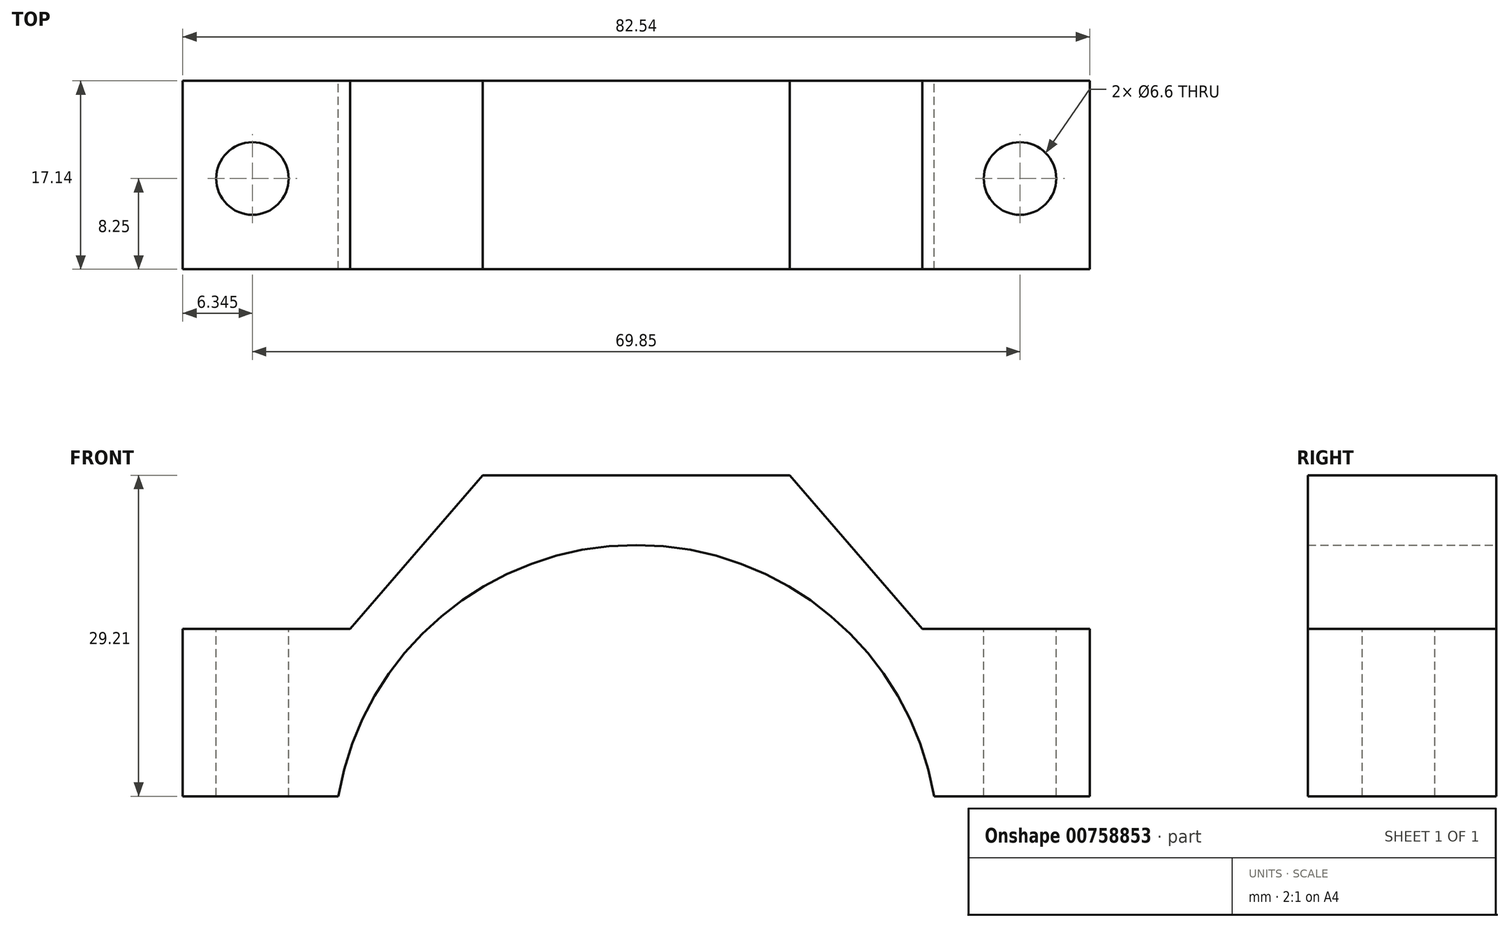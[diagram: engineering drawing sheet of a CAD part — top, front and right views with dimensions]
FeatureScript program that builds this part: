
annotation { "Feature Type Name" : "Feature", "Feature Type Description" : "" }
export const myFeature = defineFeature(function(context is Context, id is Id, definition is map)
    precondition{}
    {
        {
            var Q0;
            Q0=qCreatedBy(makeId("Front.planeOp"),FACE);
            var sketch = newSketch(context, id + "F0", { "sketchPlane" : qUnion([Q0])});
            skLineSegment(sketch, "E0", {"start": v(0, 0) * mm, "end": v(44.45, 0) * mm});
            skLineSegment(sketch, "E1", {"start": v(44.45, 0) * mm, "end": v(44.45, 17.78) * mm});
            skLineSegment(sketch, "E2", {"start": v(44.45, 17.78) * mm, "end": v(41.28, 19.05) * mm});
            skLineSegment(sketch, "E3", {"start": v(41.28, 19.05) * mm, "end": v(41.28, 52.07) * mm});
            skLineSegment(sketch, "E4", {"start": v(41.28, 52.07) * mm, "end": v(26.04, 52.07) * mm});
            skLineSegment(sketch, "E5", {"start": v(26.04, 52.07) * mm, "end": v(13.97, 66.04) * mm});
            skLineSegment(sketch, "E6", {"start": v(13.97, 66.04) * mm, "end": v(0, 66.04) * mm});
            skLineSegment(sketch, "E7.MirrorCS", {"start": v(-41.28, 19.05) * mm, "end": v(-41.28, 52.07) * mm});
            skLineSegment(sketch, "E8.MirrorCS", {"start": v(-44.45, 17.78) * mm, "end": v(-41.28, 19.05) * mm});
            skLineSegment(sketch, "E9.MirrorCS", {"start": v(-41.28, 52.07) * mm, "end": v(-26.04, 52.07) * mm});
            skLineSegment(sketch, "E10.MirrorCS", {"start": v(0, 0) * mm, "end": v(-44.45, 0) * mm});
            skLineSegment(sketch, "E11.MirrorCS", {"start": v(-13.97, 66.04) * mm, "end": v(0, 66.04) * mm});
            skLineSegment(sketch, "E12.MirrorCS", {"start": v(-26.04, 52.07) * mm, "end": v(-13.97, 66.04) * mm});
            skLineSegment(sketch, "E13.MirrorCS", {"start": v(-44.45, 0) * mm, "end": v(-44.45, 17.78) * mm});
            skCircle(sketch, "E14", {"center": v(0, 32.2) * mm, "radius": 27.5 * mm});
            skSolve(sketch);
        }
        {
            var Q0;
            Q0 = qSketchRegion(id + "F0", true);
            extrude(context, id + "F1", {"entities" : qUnion([Q0]), "depth" : 38.1 * mm, "offsetDistance" : 25.4 * mm});
        }
        {
            var Q0;
            Q0=makeQuery(id+"F1.opExtrude","CAP_FACE",FACE,{"disambiguationData":[OSD([sQuery(id+"F0.wireOp",EDGE,"E0"),sQuery(id+"F0.wireOp",EDGE,"E1"),sQuery(id+"F0.wireOp",EDGE,"E2"),sQuery(id+"F0.wireOp",EDGE,"E3"),sQuery(id+"F0.wireOp",EDGE,"E4"),sQuery(id+"F0.wireOp",EDGE,"E5"),sQuery(id+"F0.wireOp",EDGE,"E6"),sQuery(id+"F0.wireOp",EDGE,"E7.MirrorCS"),sQuery(id+"F0.wireOp",EDGE,"E8.MirrorCS"),sQuery(id+"F0.wireOp",EDGE,"E9.MirrorCS"),sQuery(id+"F0.wireOp",EDGE,"E10.MirrorCS"),sQuery(id+"F0.wireOp",EDGE,"E11.MirrorCS"),sQuery(id+"F0.wireOp",EDGE,"E12.MirrorCS"),sQuery(id+"F0.wireOp",EDGE,"E13.MirrorCS"),sQuery(id+"F0.wireOp",EDGE,"E14")])],"isStart":false});
            var sketch = newSketch(context, id + "F2", { "sketchPlane" : qUnion([Q0])});
            skLineSegment(sketch, "E15.bottom", {"start": v(-41.28, 31.75) * mm, "end": v(-22.23, 31.75) * mm});
            skLineSegment(sketch, "E15.top", {"start": v(-41.28, 36.83) * mm, "end": v(-22.23, 36.83) * mm});
            skLineSegment(sketch, "E15.left", {"start": v(-41.28, 31.75) * mm, "end": v(-41.28, 36.83) * mm});
            skLineSegment(sketch, "E15.right", {"start": v(-22.23, 31.75) * mm, "end": v(-22.23, 36.83) * mm});
            skSolve(sketch);
        }
        {
            var Q0;
            Q0 = qSketchRegion(id + "F2", true);
            extrude(context, id + "F3", {"entities" : qUnion([Q0]), "operationType" : NewBodyOperationType.REMOVE, "endBound" : BoundingType.UP_TO_NEXT, "oppositeDirection" : true, "depth" : 25.4 * mm, "offsetDistance" : 25.4 * mm});
        }
        {
            var Q0;
            Q0=makeQuery(id+"F1.opExtrude","SWEPT_FACE",FACE,{"disambiguationData":[OSD([sQuery(id+"F0.wireOp",EDGE,"E9.MirrorCS")])]});
            var sketch = newSketch(context, id + "F4", { "sketchPlane" : qUnion([Q0])});
            skLineSegment(sketch, "E16", {"start": v(-41.28, -19.05) * mm, "end": v(41.4, -19.05) * mm, "construction": true});
            skPoint(sketch, "E17", {"position": v(-34.93, -29.21) * mm});
            skPoint(sketch, "E18.MirrorP", {"position": v(-34.93, -8.89) * mm});
            skPoint(sketch, "E19.MirrorP", {"position": v(34.93, -8.89) * mm});
            skPoint(sketch, "E20.MirrorP", {"position": v(34.93, -29.21) * mm});
            skSolve(sketch);
        }
        {
            var Q0;
            Q0=sQuery(id+"F4.wireOp",VERTEX,"E18.MirrorP");
            var Q1;
            Q1=sQuery(id+"F4.wireOp",VERTEX,"E17");
            var Q2;
            Q2=sQuery(id+"F4.wireOp",VERTEX,"E19.MirrorP");
            var Q3;
            Q3=sQuery(id+"F4.wireOp",VERTEX,"E20.MirrorP");
            var Q4;
            Q4=makeQuery(id+"F1.opExtrude","SWEPT_BODY",BODY,{"disambiguationData":[OSD([sQuery(id+"F0.wireOp",EDGE,"E0"),sQuery(id+"F0.wireOp",EDGE,"E1"),sQuery(id+"F0.wireOp",EDGE,"E2"),sQuery(id+"F0.wireOp",EDGE,"E3"),sQuery(id+"F0.wireOp",EDGE,"E4"),sQuery(id+"F0.wireOp",EDGE,"E5"),sQuery(id+"F0.wireOp",EDGE,"E6"),sQuery(id+"F0.wireOp",EDGE,"E7.MirrorCS"),sQuery(id+"F0.wireOp",EDGE,"E8.MirrorCS"),sQuery(id+"F0.wireOp",EDGE,"E9.MirrorCS"),sQuery(id+"F0.wireOp",EDGE,"E10.MirrorCS"),sQuery(id+"F0.wireOp",EDGE,"E11.MirrorCS"),sQuery(id+"F0.wireOp",EDGE,"E12.MirrorCS"),sQuery(id+"F0.wireOp",EDGE,"E13.MirrorCS"),sQuery(id+"F0.wireOp",EDGE,"E14")])]});
            hole(context, id + "F5", {"style" : HoleStyle.SIMPLE, "endStyle" : HoleEndStyle.THROUGH, "standardTappedOrClearance" : lookupTablePath({ "standard" : "ISO", "fit" : "Normal", "size" : "M6", "type" : "Clearance" }), "standardBlindInLast" : lookupTablePath({ "fit" : "Standard", "standard" : "ISO", "size" : "M6", "type" : "Clearance" }), "holeDiameter" : 6.6 * mm, "majorDiameter" : 6.35 * mm, "isTappedThrough" : true, "tappedDepth" : 12.7 * mm, "tapClearance" : 3, "locations" : qUnion([Q0, Q1, Q2, Q3]), "scope" : qUnion([Q4])});
        }
        {
            var Q0;
            Q0=makeQuery(id+"F1.opExtrude","SWEPT_FACE",FACE,{"disambiguationData":[OSD([sQuery(id+"F0.wireOp",EDGE,"E0"),sQuery(id+"F0.wireOp",EDGE,"E10.MirrorCS")])]});
            var sketch = newSketch(context, id + "F6", { "sketchPlane" : qUnion([Q0])});
            skLineSegment(sketch, "E21.bottom", {"start": v(-44.45, 38.1) * mm, "end": v(44.45, 38.1) * mm});
            skLineSegment(sketch, "E21.top", {"start": v(-44.45, 0) * mm, "end": v(44.45, 0) * mm});
            skLineSegment(sketch, "E21.left", {"start": v(-44.45, 38.1) * mm, "end": v(-44.45, 0) * mm});
            skLineSegment(sketch, "E21.right", {"start": v(44.45, 38.1) * mm, "end": v(44.45, 0) * mm});
            skSolve(sketch);
        }
        {
            var Q0;
            Q0 = qSketchRegion(id + "F6", true);
            var Q1;
            Q1=makeQuery(id+"F3.boolean.opBoolean","COPY",FACE,{"derivedFrom":makeQuery(id+"F3.opExtrude","SWEPT_FACE",FACE,{"disambiguationData":[OSD([sQuery(id+"F2.wireOp",EDGE,"E15.top")])]})});
            extrude(context, id + "F7", {"entities" : qUnion([Q0]), "operationType" : NewBodyOperationType.REMOVE, "endBound" : BoundingType.UP_TO_SURFACE, "oppositeDirection" : true, "depth" : 25.4 * mm, "endBoundEntityFace" : qUnion([Q1]), "offsetDistance" : 25.4 * mm});
        }
        {
            var Q0;
            Q0=makeQuery(id+"F1.opExtrude","CAP_FACE",FACE,{"disambiguationData":[OSD([sQuery(id+"F0.wireOp",EDGE,"E0"),sQuery(id+"F0.wireOp",EDGE,"E1"),sQuery(id+"F0.wireOp",EDGE,"E2"),sQuery(id+"F0.wireOp",EDGE,"E3"),sQuery(id+"F0.wireOp",EDGE,"E4"),sQuery(id+"F0.wireOp",EDGE,"E5"),sQuery(id+"F0.wireOp",EDGE,"E6"),sQuery(id+"F0.wireOp",EDGE,"E7.MirrorCS"),sQuery(id+"F0.wireOp",EDGE,"E8.MirrorCS"),sQuery(id+"F0.wireOp",EDGE,"E9.MirrorCS"),sQuery(id+"F0.wireOp",EDGE,"E10.MirrorCS"),sQuery(id+"F0.wireOp",EDGE,"E11.MirrorCS"),sQuery(id+"F0.wireOp",EDGE,"E12.MirrorCS"),sQuery(id+"F0.wireOp",EDGE,"E13.MirrorCS"),sQuery(id+"F0.wireOp",EDGE,"E14")])],"isStart":false});
            var sketch = newSketch(context, id + "F8", { "sketchPlane" : qUnion([Q0])});
            skLineSegment(sketch, "E22.bottom", {"start": v(41.28, 66.04) * mm, "end": v(-41.28, 66.04) * mm});
            skLineSegment(sketch, "E22.top", {"start": v(41.28, 36.83) * mm, "end": v(-41.28, 36.83) * mm});
            skLineSegment(sketch, "E22.left", {"start": v(41.28, 66.04) * mm, "end": v(41.28, 36.83) * mm});
            skLineSegment(sketch, "E22.right", {"start": v(-41.28, 66.04) * mm, "end": v(-41.28, 36.83) * mm});
            skSolve(sketch);
        }
        {
            var Q0;
            Q0 = qSketchRegion(id + "F8", true);
            extrude(context, id + "F9", {"entities" : qUnion([Q0]), "operationType" : NewBodyOperationType.REMOVE, "oppositeDirection" : true, "depth" : 20.95 * mm, "offsetDistance" : 25.4 * mm});
        }
    });
